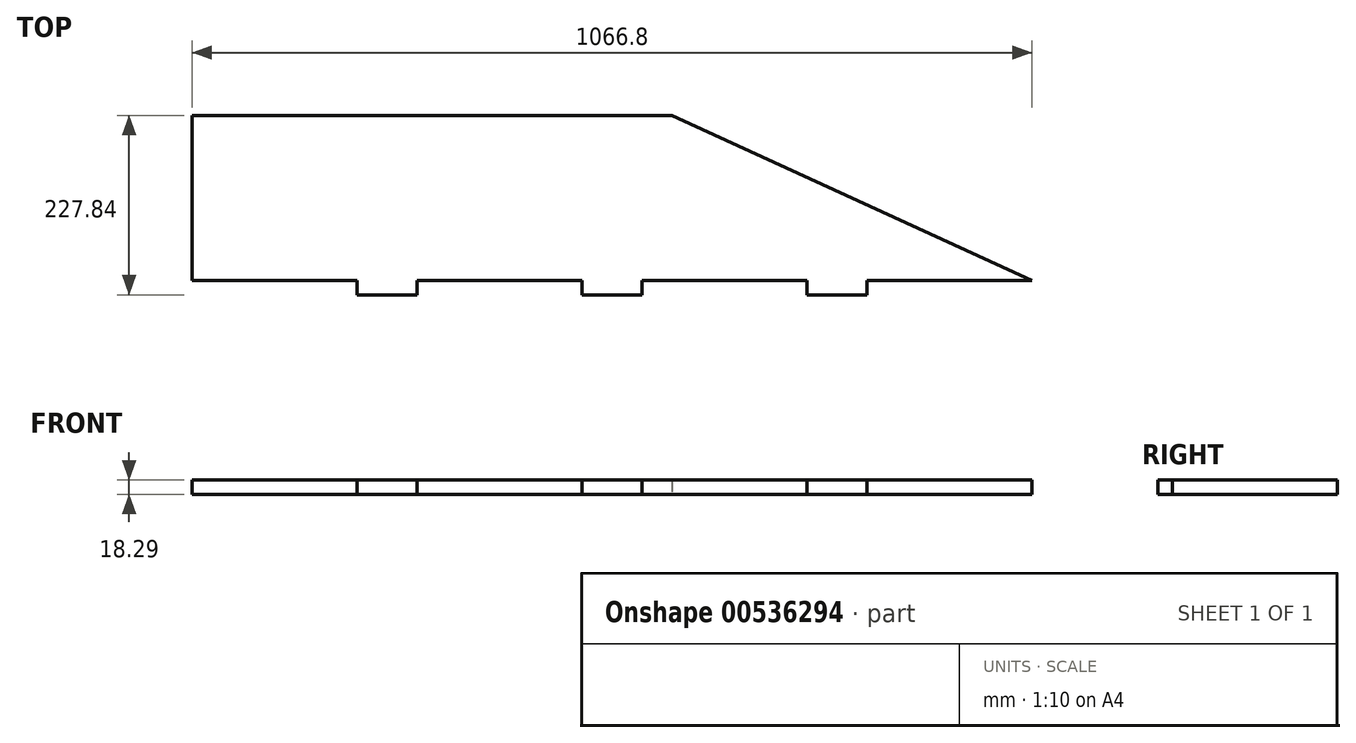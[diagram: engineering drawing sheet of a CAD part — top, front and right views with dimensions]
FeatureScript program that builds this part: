
annotation { "Feature Type Name" : "Feature", "Feature Type Description" : "" }
export const myFeature = defineFeature(function(context is Context, id is Id, definition is map)
    precondition{}
    {
        {
            var Q0;
            Q0=qCreatedBy(makeId("Top.planeOp"),FACE);
            var sketch = newSketch(context, id + "F0", { "sketchPlane" : qUnion([Q0])});
            skLineSegment(sketch, "E0", {"start": v(-1067.61, -32.65) * mm, "end": v(-858.06, -32.65) * mm});
            skLineSegment(sketch, "E1.top", {"start": v(-858.06, -50.94) * mm, "end": v(-781.86, -50.94) * mm});
            skLineSegment(sketch, "E1.left", {"start": v(-858.06, -32.65) * mm, "end": v(-858.06, -50.94) * mm});
            skLineSegment(sketch, "E1.right", {"start": v(-781.86, -32.65) * mm, "end": v(-781.86, -50.94) * mm});
            skLineSegment(sketch, "E2", {"start": v(-781.86, -32.65) * mm, "end": v(-572.31, -32.65) * mm});
            skLineSegment(sketch, "E3.top", {"start": v(-572.31, -50.94) * mm, "end": v(-496.11, -50.94) * mm});
            skLineSegment(sketch, "E3.left", {"start": v(-572.31, -32.65) * mm, "end": v(-572.31, -50.94) * mm});
            skLineSegment(sketch, "E3.right", {"start": v(-496.11, -32.65) * mm, "end": v(-496.11, -50.94) * mm});
            skLineSegment(sketch, "E4", {"start": v(-496.11, -32.65) * mm, "end": v(-286.56, -32.65) * mm});
            skLineSegment(sketch, "E5.top", {"start": v(-286.56, -50.94) * mm, "end": v(-210.36, -50.94) * mm});
            skLineSegment(sketch, "E5.left", {"start": v(-286.56, -32.65) * mm, "end": v(-286.56, -50.94) * mm});
            skLineSegment(sketch, "E5.right", {"start": v(-210.36, -32.65) * mm, "end": v(-210.36, -50.94) * mm});
            skLineSegment(sketch, "E6", {"start": v(-210.36, -32.65) * mm, "end": v(-0.81, -32.65) * mm});
            skLineSegment(sketch, "E7", {"start": v(-1067.61, -32.65) * mm, "end": v(-1067.61, 176.9) * mm});
            skLineSegment(sketch, "E8", {"start": v(-1067.61, 176.9) * mm, "end": v(-458.01, 176.9) * mm});
            skLineSegment(sketch, "E9", {"start": v(-458.01, 176.9) * mm, "end": v(-0.81, -32.65) * mm});
            skSolve(sketch);
        }
        {
            var Q0;
            Q0=makeQuery(id+"F0.imprint","IMPRINT",FACE,{"disambiguationData":[TD([[makeQuery(id+"F0.imprint","IMPRINT",EDGE,{"derivedFrom":sQuery(id+"F0.wireOp",EDGE,"E0")}),1.0]])]});
            extrude(context, id + "F1", {"entities" : qUnion([Q0]), "depth" : 18.29 * mm, "offsetDistance" : 25.4 * mm});
        }
    });
